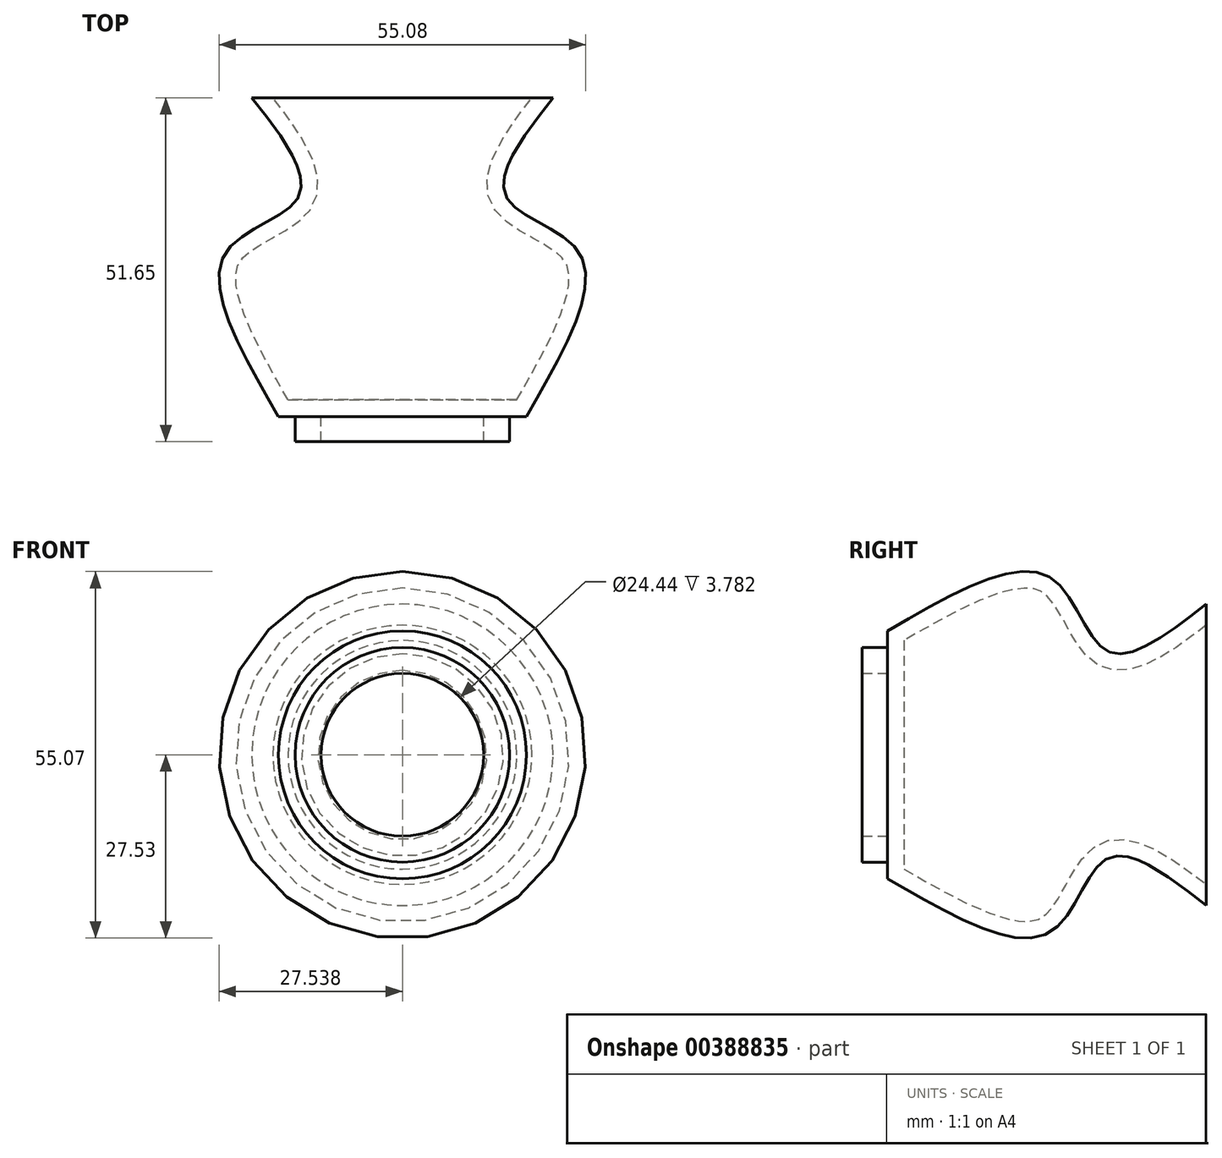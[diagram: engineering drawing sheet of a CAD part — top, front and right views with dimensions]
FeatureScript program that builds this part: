
annotation { "Feature Type Name" : "Feature", "Feature Type Description" : "" }
export const myFeature = defineFeature(function(context is Context, id is Id, definition is map)
    precondition{}
    {
        {
            var Q0;
            Q0=qCreatedBy(makeId("Top.planeOp"),FACE);
            var sketch = newSketch(context, id + "F0", { "sketchPlane" : qUnion([Q0])});
            skLineSegment(sketch, "E0", {"start": v(15.96, -17.38) * mm, "end": v(15.96, -65.25) * mm});
            skLineSegment(sketch, "E1", {"start": v(15.96, -65.25) * mm, "end": v(28.18, -65.25) * mm});
            skLineSegment(sketch, "E2", {"start": v(28.18, -65.25) * mm, "end": v(28.18, -69.03) * mm});
            skLineSegment(sketch, "E3", {"start": v(28.18, -69.03) * mm, "end": v(32.07, -69.03) * mm});
            skLineSegment(sketch, "E4", {"start": v(32.07, -69.03) * mm, "end": v(32.07, -65.25) * mm});
            skLineSegment(sketch, "E5", {"start": v(32.07, -65.25) * mm, "end": v(34.57, -65.25) * mm});
            skLineSegment(sketch, "E6", {"start": v(15.96, -17.38) * mm, "end": v(38.59, -17.38) * mm});
            skFitSpline(sketch, "E7", {"points": [v(38.59, -17.38) * mm, v(31.56, -32.3) * mm, v(42.6, -40.82) * mm, v(34.57, -65.25) * mm], "startDerivative": vector(-42.18, -54.08) * mm, "endDerivative": vector(-42.44, -73.17) * mm});
            skSolve(sketch);
        }
        {
            var Q0;
            Q0=makeQuery(id+"F0.imprint","IMPRINT",FACE,{"disambiguationData":[TD([[makeQuery(id+"F0.imprint","IMPRINT",EDGE,{"derivedFrom":sQuery(id+"F0.wireOp",EDGE,"E0")}),1.0]])]});
            var Q1;
            Q1=sQuery(id+"F0.wireOp",EDGE,"E0");
            revolve(context, id + "F1", {"entities" : qUnion([Q0]), "axis" : qUnion([Q1]), "revolveType" : RevolveType.FULL});
        }
        {
            var Q0;
            Q0=makeQuery(id+"F1.opRevolve","SWEPT_FACE",FACE,{"disambiguationData":[OSD([sQuery(id+"F0.wireOp",EDGE,"E6")])]});
            shell(context, id + "F2", {"entities" : qUnion([Q0]), "thickness" : 2.5 * mm});
        }
    });
